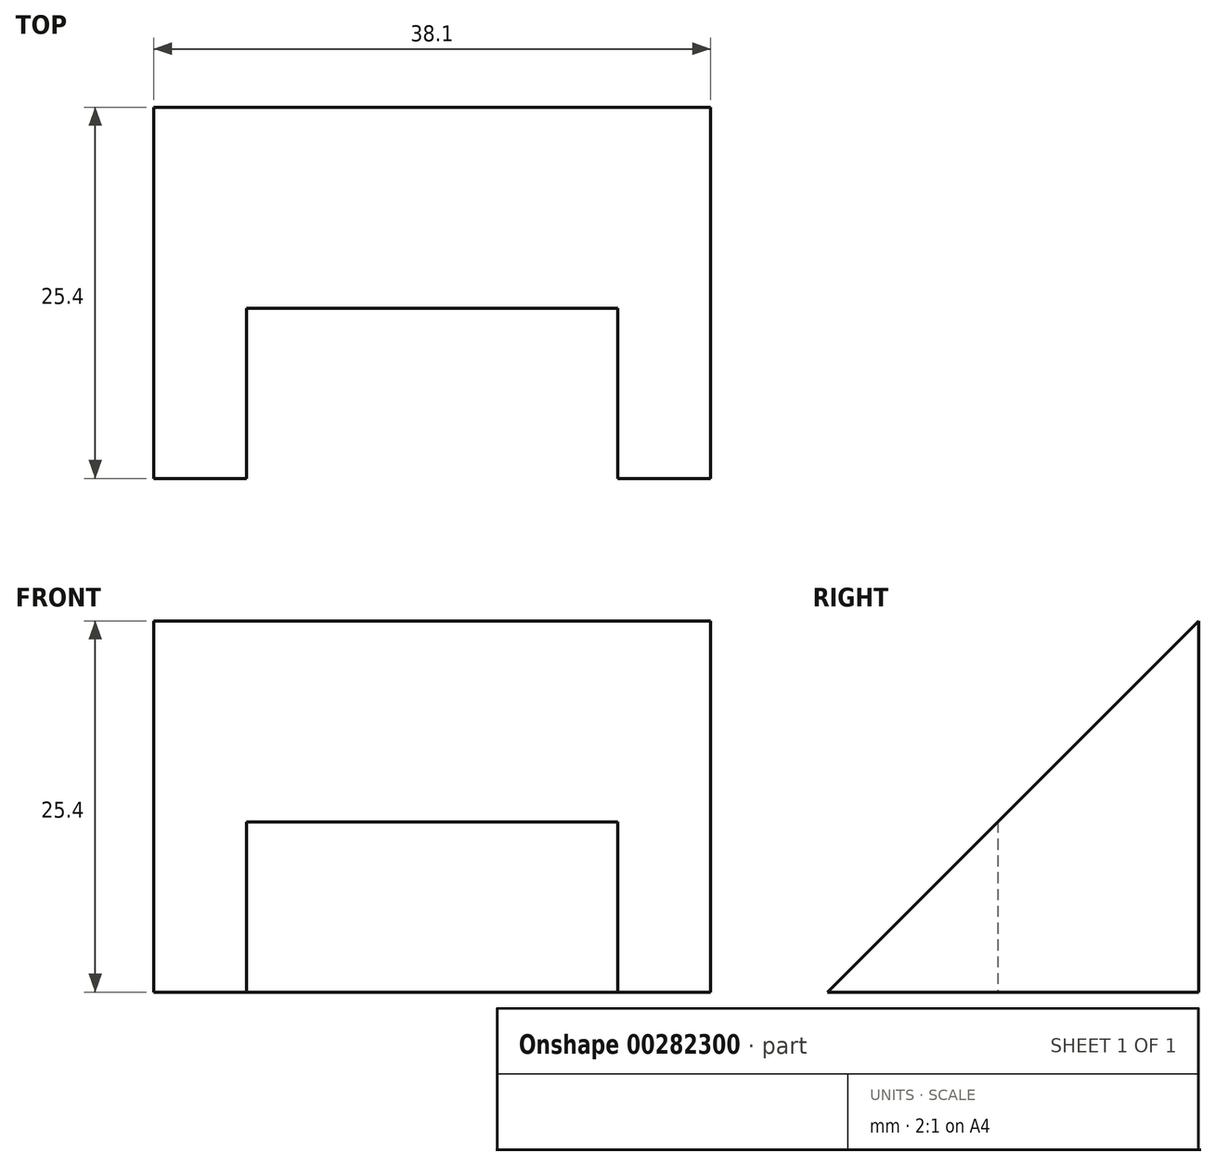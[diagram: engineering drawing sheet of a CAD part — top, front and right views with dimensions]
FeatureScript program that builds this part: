
annotation { "Feature Type Name" : "Feature", "Feature Type Description" : "" }
export const myFeature = defineFeature(function(context is Context, id is Id, definition is map)
    precondition{}
    {
        {
            var Q0;
            Q0=qCreatedBy(makeId("Right.planeOp"),FACE);
            var sketch = newSketch(context, id + "F0", { "sketchPlane" : qUnion([Q0])});
            skLineSegment(sketch, "E0", {"start": v(0, 0) * mm, "end": v(-25.4, 0) * mm});
            skLineSegment(sketch, "E1", {"start": v(-25.4, 0) * mm, "end": v(0, 25.4) * mm});
            skLineSegment(sketch, "E2", {"start": v(0, 25.4) * mm, "end": v(0, 0) * mm});
            skSolve(sketch);
        }
        {
            var Q0;
            Q0 = qSketchRegion(id + "F0", true);
            extrude(context, id + "F1", {"entities" : qUnion([Q0]), "oppositeDirection" : true, "depth" : 38.1 * mm});
        }
        {
            var Q0;
            Q0=qCreatedBy(makeId("Top.planeOp"),FACE);
            var sketch = newSketch(context, id + "F2", { "sketchPlane" : qUnion([Q0])});
            skLineSegment(sketch, "E3.bottom", {"start": v(-31.75, -25.4) * mm, "end": v(-6.35, -25.4) * mm});
            skLineSegment(sketch, "E3.top", {"start": v(-31.75, -13.75) * mm, "end": v(-6.35, -13.75) * mm});
            skLineSegment(sketch, "E3.left", {"start": v(-31.75, -25.4) * mm, "end": v(-31.75, -13.75) * mm});
            skLineSegment(sketch, "E3.right", {"start": v(-6.35, -25.4) * mm, "end": v(-6.35, -13.75) * mm});
            skSolve(sketch);
        }
        {
            var Q0;
            Q0 = qSketchRegion(id + "F2", true);
            extrude(context, id + "F3", {"entities" : qUnion([Q0]), "operationType" : NewBodyOperationType.REMOVE, "depth" : 25.4 * mm});
        }
    });
